# Revit family: Maxlogic manual call poınt resettable (Low IP)
name_source: partatom
category: Fire Alarm Devices
units: mm (PartAtom-declared; Revit-internal decimal feet)

## family parameters
Cut with Voids When Loaded = No
Host = Face
Maintain Annotation Orientation = Yes
OmniClass Number = 23.85.30.21
OmniClass Title = Environmental Detection/Registration
Part Type = Normal
Room Calculation Point = No
Round Connector Dimension = Use Diameter
Shared = No

## types (5) — shared parameters
Code Performance = EN 54-11
Color = Red
Fax Number = (+)90 216 466 45 10
Installation Manual = https://mavilielektronik.com
Main Material = Red Plastic ABS
Manufacturer = Mavili Elektronik Ticaret A.Ş.
Model = MaxLogic
Mounting height = 140 cm above from ground (+/-200mm)
Mounting surface = wall mount
Nominal  Width = 87 mm
Nominal Depth = 58 mm
Nominal Height = 91 mm
Operatonal Voltage (default) = 24 V/DC
Secondary Material = Plastic
URL = https://www.mavili.com.tr
Warranty Duration Labor = 2
Warranty Duration Parts = 2
Warranty Duration Unit = Year
zero-valued in all types: Cost, Default Elevation

## per-type parameters (varying)
| type | Description | Device Adress Setup | Manual Call Point Led | Operating temperature | Operating voltage range | Product Code | Protection Sign | Protective Cover | Public Works Pose Number | Weight |
| Maxlogic Conventional fire alarm call point, resettable | Conventional fire alarm call point, resettable |  | No | (-10°C) - (+55°C) | 10-30 V/DC | ML-2710 | IP22D | ML-0710 | 830-102 | 140 gr. |
| Maxlogic Addressable manual call point, resettable, two-terminal back box | Addressable manual call point, resettable, two-terminal back box | The address is given to devices by addressable programmer | Yes | (-10°C) - (+55°C) | 18-33 V/DC | ML-1710 | IP22D | ML-0710 | 833-557 | 150 gr. |
| Maxlogic Addressable manual call point, short circuit isolator, resettable | Addressable manual call point, short circuit isolator, resettable | The address is given to devices by addressable programmer | Yes | (-10°C) - (+55°C) | 10-30 V/DC | ML-1710.SCI | IP22D | ML-0710 | 833-558 | 150 gr. |
| Maxlogic Conventional Manual Call Point, Resettable, Weatherproof (IP65) | Conventional Manual Call Point, Resettable, Weatherproof (IP65) |  | No | (-25°C) - (+70°C) | 10-30 V/DC | ML-2730 | IP65 | ML-0710 | 35.415.1420 | 270 gr. |
| Maxlogic Conventional Manual Call Point, Resettable, Weatherproof (IP65), NC/NO Contact | Conventional Manual Call Point, Resettable, Weatherproof (IP65), NC/NO Contact |  | No | (-25°C) - (+70°C) | 10-30 V/DC | ML-2731 | IP65 |  | 35.415.1420 | 270 gr. |

## geometry (parser evidence)
native form markers: Sweep x2
no freeform markers — native parametric forms only
